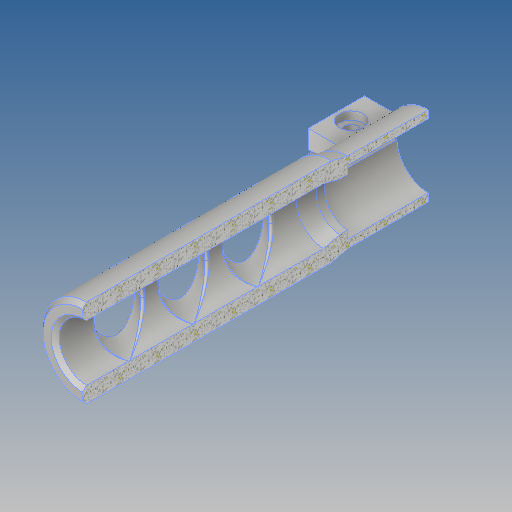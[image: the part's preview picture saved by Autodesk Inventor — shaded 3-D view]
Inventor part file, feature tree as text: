
AUTODESK INVENTOR PART (.ipt)
format: ipt  version: 2019 (Build 230136000, 136)  size: 869,376 bytes
history: native  units: mm
features: other x6, sketch x6, projected_geometry x6, extrude x3, mirror x2, hole x2, fillet x1, pattern_linear x1
ambient origin geometry x8: Origin, YZ Plane, XZ Plane, XY Plane, X Axis, Y Axis, Z Axis, Center Point
bodies: Solide1 (feature_tree)
feature tree (27):
  other  "Révolution1"
  other  "Plan de construction2"
  other  "Plan de construction3"
  extrude  "Extrusion1"  Depth=16.0mm
  fillet  "Congé1"  Radius=2.0mm
  mirror  "Symétrie1"
  pattern_linear  "Réseau rectangulaire1"  Spacing1=14.0mm  [1 undecoded]
  other  "Plan de construction4"
  extrude  "Extrusion2"  Depth=4.0mm
  mirror  "Symétrie2"
  extrude  "Extrusion3"  Depth=2.0mm
  hole  "Perçage1"  [1 undecoded]
  hole  "Perçage2"  [1 undecoded]
  sketch  "Esquisse1"
  other  "Plan de construction1"
  other  "Axe de construction1"
  sketch  "Esquisse2"
  projected_geometry  "Boucle projetée1"
  sketch  "Esquisse3"
  projected_geometry  "Boucle projetée2"
  sketch  "Esquisse4"
  projected_geometry  "Boucle projetée3"
  projected_geometry  "Boucle projetée4"
  sketch  "Esquisse5"
  projected_geometry  "Boucle projetée5"
  projected_geometry  "Boucle projetée6"
  sketch  "Esquisse6"
note: 3 required parameter values undecoded (feature->parameter linkage not recoverable at this tier; creation-order binding heuristic only, values carry confidence <= 0.55)
